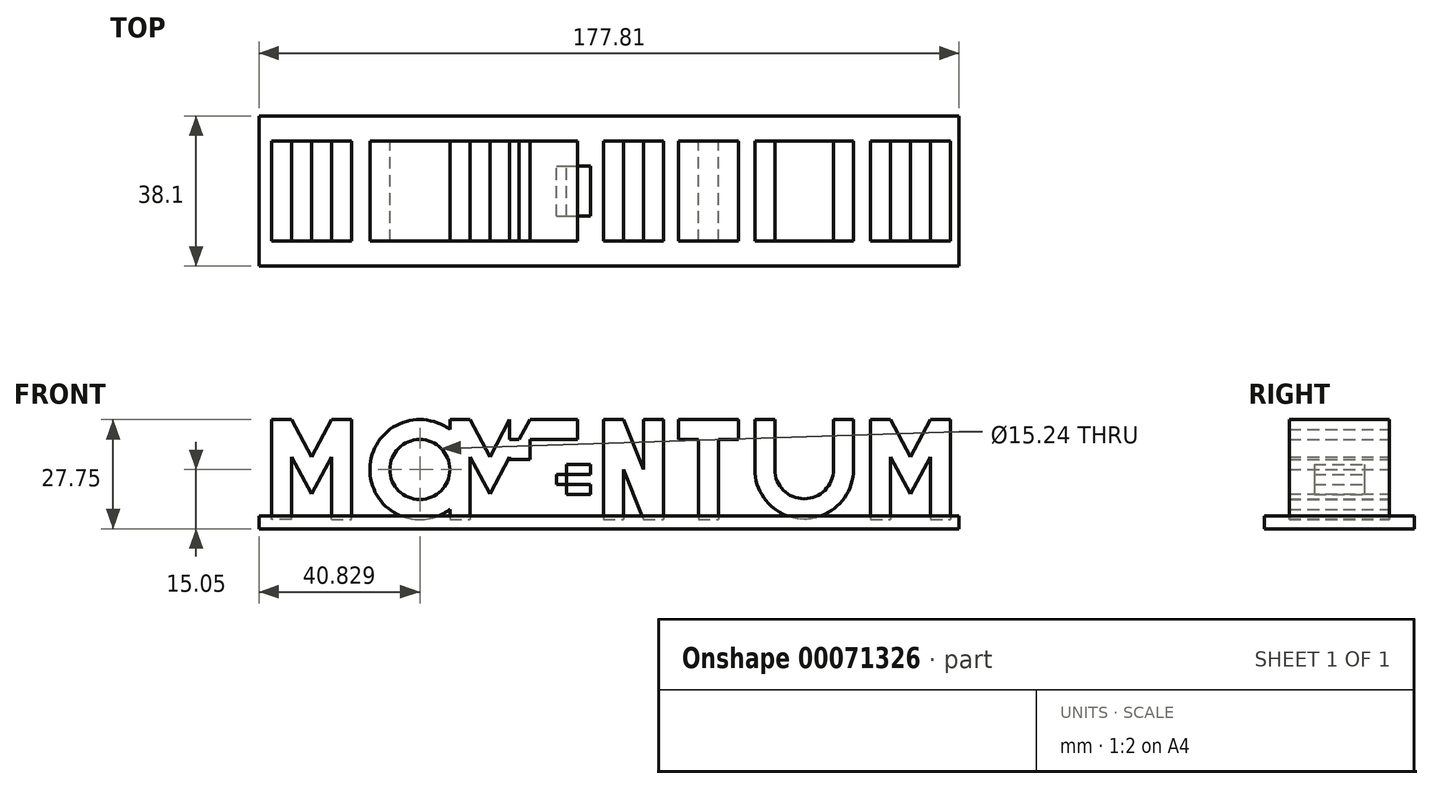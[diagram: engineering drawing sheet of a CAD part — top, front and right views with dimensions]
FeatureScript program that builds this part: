
annotation { "Feature Type Name" : "Feature", "Feature Type Description" : "" }
export const myFeature = defineFeature(function(context is Context, id is Id, definition is map)
    precondition{}
    {
        {
            var Q0;
            Q0=qCreatedBy(makeId("Front.planeOp"),FACE);
            var sketch = newSketch(context, id + "F0", { "sketchPlane" : qUnion([Q0])});
            skLineSegment(sketch, "E0.rect.bottom", {"start": v(-39.63, -6.35) * mm, "end": v(-42.17, -6.35) * mm});
            skLineSegment(sketch, "E0.rect.top", {"start": v(-39.63, 6.35) * mm, "end": v(-42.17, 6.35) * mm});
            skLineSegment(sketch, "E0.rect.left", {"start": v(-39.63, -6.35) * mm, "end": v(-39.63, 6.35) * mm});
            skLineSegment(sketch, "E0.rect.right", {"start": v(-42.17, -6.35) * mm, "end": v(-42.17, 6.35) * mm});
            skPoint(sketch, "E0.rect.middle", {"position": v(-40.9, 0) * mm});
            skLineSegment(sketch, "E1", {"start": v(-42.17, 6.35) * mm, "end": v(3.15, 6.35) * mm});
            skPoint(sketch, "E1.endSnap0", {"position": v(-40.9, 6.35) * mm});
            skLineSegment(sketch, "E2", {"start": v(-42.17, -6.35) * mm, "end": v(48.91, -6.35) * mm});
            skPoint(sketch, "E2.endSnap0", {"position": v(-40.9, -6.35) * mm});
            skLineSegment(sketch, "E3", {"start": v(-37.1, 6.35) * mm, "end": v(-37.1, -6.35) * mm});
            skLineSegment(sketch, "E4.MirrorCS", {"start": v(-34.55, -6.35) * mm, "end": v(-34.55, 6.35) * mm});
            skLineSegment(sketch, "E5.MirrorCS", {"start": v(-32.01, -6.35) * mm, "end": v(-32.01, 6.35) * mm});
            skLineSegment(sketch, "E6", {"start": v(-42.17, 6.35) * mm, "end": v(-37.1, -3.1) * mm});
            skLineSegment(sketch, "E7", {"start": v(-39.63, 6.35) * mm, "end": v(-37.1, 1.63) * mm});
            skLineSegment(sketch, "E8", {"start": v(-37.1, 1.63) * mm, "end": v(-34.55, 6.35) * mm});
            skLineSegment(sketch, "E9", {"start": v(-32.01, 6.35) * mm, "end": v(-37.1, -3.1) * mm});
            skCircle(sketch, "E10", {"center": v(-23.32, 0) * mm, "radius": 6.35 * mm});
            skCircle(sketch, "E11", {"center": v(-23.32, 0) * mm, "radius": 3.8 * mm});
            skLineSegment(sketch, "E12", {"start": v(-19.51, 0) * mm, "end": v(-16.97, 0) * mm});
            skLineSegment(sketch, "E13", {"start": v(-19.51, 6.35) * mm, "end": v(-19.51, -6.35) * mm});
            skLineSegment(sketch, "E14", {"start": v(-16.97, 6.35) * mm, "end": v(-16.97, -6.35) * mm});
            skLineSegment(sketch, "E15", {"start": v(-14.43, 6.35) * mm, "end": v(-14.43, -6.35) * mm});
            skLineSegment(sketch, "E16", {"start": v(-11.9, 6.35) * mm, "end": v(-11.9, -6.35) * mm});
            skLineSegment(sketch, "E17", {"start": v(-9.35, 6.35) * mm, "end": v(-9.35, -6.35) * mm});
            skLineSegment(sketch, "E18", {"start": v(-19.51, 6.35) * mm, "end": v(-14.43, -3.1) * mm});
            skLineSegment(sketch, "E19", {"start": v(-14.43, -3.1) * mm, "end": v(-9.35, 6.35) * mm});
            skLineSegment(sketch, "E20", {"start": v(-16.97, 6.35) * mm, "end": v(-14.43, 1.62) * mm});
            skLineSegment(sketch, "E21", {"start": v(-14.43, 1.62) * mm, "end": v(-11.9, 6.35) * mm});
            skLineSegment(sketch, "E22", {"start": v(3.15, 6.35) * mm, "end": v(48.32, 6.35) * mm});
            skLineSegment(sketch, "E23.bottom", {"start": v(-11.9, 6.35) * mm, "end": v(-3.3, 6.35) * mm});
            skLineSegment(sketch, "E23.top", {"start": v(-11.9, 3.81) * mm, "end": v(-3.3, 3.81) * mm});
            skLineSegment(sketch, "E23.left", {"start": v(-11.9, 6.35) * mm, "end": v(-11.9, 3.81) * mm});
            skLineSegment(sketch, "E23.right", {"start": v(-3.3, 6.35) * mm, "end": v(-3.3, 3.81) * mm});
            skLineSegment(sketch, "E24.bottom", {"start": v(-11.9, 1.27) * mm, "end": v(-3.3, 1.27) * mm});
            skLineSegment(sketch, "E24.top", {"start": v(-11.9, -1.27) * mm, "end": v(-3.3, -1.27) * mm});
            skLineSegment(sketch, "E24.left", {"start": v(-11.9, 1.27) * mm, "end": v(-11.9, -1.27) * mm});
            skLineSegment(sketch, "E24.right", {"start": v(-3.3, 1.27) * mm, "end": v(-3.3, -1.27) * mm});
            skLineSegment(sketch, "E25.bottom", {"start": v(-11.9, -6.35) * mm, "end": v(-3.3, -6.35) * mm});
            skLineSegment(sketch, "E25.top", {"start": v(-11.9, -3.8) * mm, "end": v(-3.3, -3.8) * mm});
            skLineSegment(sketch, "E25.left", {"start": v(-11.9, -6.35) * mm, "end": v(-11.9, -3.8) * mm});
            skLineSegment(sketch, "E25.right", {"start": v(-3.3, -6.35) * mm, "end": v(-3.3, -3.8) * mm});
            skLineSegment(sketch, "E26", {"start": v(0, 6.35) * mm, "end": v(0, -6.35) * mm});
            skLineSegment(sketch, "E27", {"start": v(2.54, 6.35) * mm, "end": v(2.54, -6.35) * mm});
            skLineSegment(sketch, "E28", {"start": v(5.08, 6.35) * mm, "end": v(5.08, -6.35) * mm});
            skLineSegment(sketch, "E29", {"start": v(7.62, 6.35) * mm, "end": v(7.62, -6.35) * mm});
            skLineSegment(sketch, "E30", {"start": v(0, 6.35) * mm, "end": v(5.08, -6.35) * mm});
            skLineSegment(sketch, "E31", {"start": v(2.54, 6.35) * mm, "end": v(7.62, -6.35) * mm});
            skLineSegment(sketch, "E32.bottom", {"start": v(12.07, 6.35) * mm, "end": v(14.6, 6.35) * mm});
            skLineSegment(sketch, "E32.top", {"start": v(12.07, -6.35) * mm, "end": v(14.6, -6.35) * mm});
            skLineSegment(sketch, "E32.left", {"start": v(12.07, 6.35) * mm, "end": v(12.07, -6.35) * mm});
            skLineSegment(sketch, "E32.right", {"start": v(14.6, 6.35) * mm, "end": v(14.6, -6.35) * mm});
            skLineSegment(sketch, "E33.bottom", {"start": v(9.53, 6.35) * mm, "end": v(17.15, 6.35) * mm});
            skLineSegment(sketch, "E33.top", {"start": v(9.53, 3.81) * mm, "end": v(17.15, 3.81) * mm});
            skLineSegment(sketch, "E33.left", {"start": v(9.53, 6.35) * mm, "end": v(9.53, 3.81) * mm});
            skLineSegment(sketch, "E33.right", {"start": v(17.15, 6.35) * mm, "end": v(17.15, 3.81) * mm});
            skArc(sketch, "E34", {"start": v(19.25, 0) * mm, "mid": v(25.5, -6.25) * mm, "end": v(31.76, 0) * mm});
            skArc(sketch, "E35", {"start": v(21.79, 0) * mm, "mid": v(25.5, -3.71) * mm, "end": v(29.22, 0) * mm});
            skLineSegment(sketch, "E36", {"start": v(19.25, 0) * mm, "end": v(19.25, 6.35) * mm});
            skLineSegment(sketch, "E37", {"start": v(21.79, 0) * mm, "end": v(21.79, 6.35) * mm});
            skLineSegment(sketch, "E38", {"start": v(29.22, 0) * mm, "end": v(29.22, 6.35) * mm});
            skLineSegment(sketch, "E39", {"start": v(31.76, 0) * mm, "end": v(31.76, 6.35) * mm});
            skLineSegment(sketch, "E40", {"start": v(33.92, 6.35) * mm, "end": v(33.92, -6.35) * mm});
            skLineSegment(sketch, "E41", {"start": v(36.46, 6.35) * mm, "end": v(36.46, -6.35) * mm});
            skLineSegment(sketch, "E42", {"start": v(39, 6.35) * mm, "end": v(39, -6.35) * mm});
            skLineSegment(sketch, "E43", {"start": v(41.54, 6.35) * mm, "end": v(41.54, -6.35) * mm});
            skLineSegment(sketch, "E44", {"start": v(44.08, 6.35) * mm, "end": v(44.08, -6.35) * mm});
            skLineSegment(sketch, "E45", {"start": v(33.92, 6.35) * mm, "end": v(39, -3.1) * mm});
            skLineSegment(sketch, "E46", {"start": v(39, -3.1) * mm, "end": v(44.08, 6.35) * mm});
            skLineSegment(sketch, "E47", {"start": v(36.46, 6.35) * mm, "end": v(39, 1.63) * mm});
            skLineSegment(sketch, "E48", {"start": v(39, 1.63) * mm, "end": v(41.54, 6.35) * mm});
            skSolve(sketch);
        }
        {
            var Q0;
            {var subQ5=sQuery(id+"F0.wireOp",EDGE,"E0.rect.right");Q0=makeQuery(id+"F0.imprint","IMPRINT",FACE,{"disambiguationData":[TD([[makeQuery(id+"F0.imprint","IMPRINT",EDGE,{"derivedFrom":subQ5}),-1.0]])]});}
            var Q1;
            {var subQ1=sQuery(id+"F0.wireOp",EDGE,"E0.rect.left");var subQ3=sQuery(id+"F0.wireOp",EDGE,"E6");var subQ4=makeQuery(id+"F0.imprint","INTERSECT",VERTEX,{"derivedFrom":[subQ1,subQ3]});Q1=makeQuery(id+"F0.imprint","IMPRINT",FACE,{"disambiguationData":[TD([[makeQuery(id+"F0.imprint","IMPRINT",EDGE,{"disambiguationData":[TD([[subQ4,-1.0]])],"derivedFrom":subQ1}),1.0]])]});}
            var Q2;
            {var subQ0=sQuery(id+"F0.wireOp",EDGE,"E7");Q2=makeQuery(id+"F0.imprint","IMPRINT",FACE,{"disambiguationData":[TD([[makeQuery(id+"F0.imprint","IMPRINT",EDGE,{"derivedFrom":subQ0}),-1.0]])]});}
            var Q3;
            {var subQ3=sQuery(id+"F0.wireOp",EDGE,"E8");Q3=makeQuery(id+"F0.imprint","IMPRINT",FACE,{"disambiguationData":[TD([[makeQuery(id+"F0.imprint","IMPRINT",EDGE,{"derivedFrom":subQ3}),-1.0]])]});}
            var Q4;
            {var subQ0=sQuery(id+"F0.wireOp",EDGE,"E4.MirrorCS");var subQ3=sQuery(id+"F0.wireOp",EDGE,"E9");var subQ5=makeQuery(id+"F0.imprint","INTERSECT",VERTEX,{"derivedFrom":[subQ0,subQ3]});Q4=makeQuery(id+"F0.imprint","IMPRINT",FACE,{"disambiguationData":[TD([[makeQuery(id+"F0.imprint","IMPRINT",EDGE,{"disambiguationData":[TD([[subQ5,-1.0]])],"derivedFrom":subQ0}),-1.0]])]});}
            var Q5;
            {var subQ3=sQuery(id+"F0.wireOp",EDGE,"E5.MirrorCS");Q5=makeQuery(id+"F0.imprint","IMPRINT",FACE,{"disambiguationData":[TD([[makeQuery(id+"F0.imprint","IMPRINT",EDGE,{"derivedFrom":subQ3}),1.0]])]});}
            var Q6;
            {var subQ0=sQuery(id+"F0.wireOp",EDGE,"E11");Q6=makeQuery(id+"F0.imprint","IMPRINT",FACE,{"disambiguationData":[TD([[makeQuery(id+"F0.imprint","IMPRINT",EDGE,{"derivedFrom":subQ0}),-1.0]])]});}
            var Q7;
            {var subQ0=sQuery(id+"F0.wireOp",EDGE,"E12");Q7=makeQuery(id+"F0.imprint","IMPRINT",FACE,{"disambiguationData":[TD([[makeQuery(id+"F0.imprint","IMPRINT",EDGE,{"derivedFrom":subQ0}),1.0]])]});}
            var Q8;
            {var subQ0=sQuery(id+"F0.wireOp",EDGE,"E12");Q8=makeQuery(id+"F0.imprint","IMPRINT",FACE,{"disambiguationData":[TD([[makeQuery(id+"F0.imprint","IMPRINT",EDGE,{"derivedFrom":subQ0}),-1.0]])]});}
            var Q9;
            {var subQ0=sQuery(id+"F0.wireOp",EDGE,"E13");var subQ1=sQuery(id+"F0.wireOp",EDGE,"E2");var subQ2=makeQuery(id+"F0.imprint","INTERSECT",VERTEX,{"derivedFrom":[subQ1,subQ0]});Q9=makeQuery(id+"F0.imprint","IMPRINT",FACE,{"disambiguationData":[TD([[makeQuery(id+"F0.imprint","IMPRINT",EDGE,{"disambiguationData":[TD([[subQ2,-1.0]])],"derivedFrom":subQ1}),1.0]])]});}
            var Q10;
            {var subQ0=sQuery(id+"F0.wireOp",EDGE,"E18");var subQ3=sQuery(id+"F0.wireOp",EDGE,"E14");var subQ5=makeQuery(id+"F0.imprint","INTERSECT",VERTEX,{"derivedFrom":[subQ3,subQ0]});Q10=makeQuery(id+"F0.imprint","IMPRINT",FACE,{"disambiguationData":[TD([[makeQuery(id+"F0.imprint","IMPRINT",EDGE,{"disambiguationData":[TD([[subQ5,1.0]])],"derivedFrom":subQ3}),-1.0]])]});}
            var Q11;
            {var subQ1=sQuery(id+"F0.wireOp",EDGE,"E10");var subQ3=sQuery(id+"F0.wireOp",EDGE,"E13");var subQ4=makeQuery(id+"F0.imprint","INTERSECT",VERTEX,{"disambiguationData":[OD(0.0)],"derivedFrom":[subQ1,subQ3]});Q11=makeQuery(id+"F0.imprint","IMPRINT",FACE,{"disambiguationData":[TD([[makeQuery(id+"F0.imprint","IMPRINT",EDGE,{"disambiguationData":[TD([[subQ4,1.0]])],"derivedFrom":subQ1}),-1.0]])]});}
            var Q12;
            {var subQ0=sQuery(id+"F0.wireOp",EDGE,"E20");Q12=makeQuery(id+"F0.imprint","IMPRINT",FACE,{"disambiguationData":[TD([[makeQuery(id+"F0.imprint","IMPRINT",EDGE,{"derivedFrom":subQ0}),-1.0]])]});}
            var Q13;
            {var subQ5=sQuery(id+"F0.wireOp",EDGE,"E21");Q13=makeQuery(id+"F0.imprint","IMPRINT",FACE,{"disambiguationData":[TD([[makeQuery(id+"F0.imprint","IMPRINT",EDGE,{"derivedFrom":subQ5}),-1.0]])]});}
            var Q14;
            {var subQ5=sQuery(id+"F0.wireOp",EDGE,"E23.left");Q14=makeQuery(id+"F0.imprint","IMPRINT",FACE,{"disambiguationData":[TD([[makeQuery(id+"F0.imprint","IMPRINT",EDGE,{"derivedFrom":subQ5}),1.0]])]});}
            var Q15;
            {var subQ1=sQuery(id+"F0.wireOp",EDGE,"E16");var subQ3=sQuery(id+"F0.wireOp",EDGE,"E19");var subQ4=makeQuery(id+"F0.imprint","INTERSECT",VERTEX,{"derivedFrom":[subQ1,subQ3]});Q15=makeQuery(id+"F0.imprint","IMPRINT",FACE,{"disambiguationData":[TD([[makeQuery(id+"F0.imprint","IMPRINT",EDGE,{"disambiguationData":[TD([[subQ4,-1.0]])],"derivedFrom":subQ3}),1.0]])]});}
            var Q16;
            {var subQ5=sQuery(id+"F0.wireOp",EDGE,"E23.right");Q16=makeQuery(id+"F0.imprint","IMPRINT",FACE,{"disambiguationData":[TD([[makeQuery(id+"F0.imprint","IMPRINT",EDGE,{"derivedFrom":subQ5}),-1.0]])]});}
            var Q17;
            {var subQ0=sQuery(id+"F0.wireOp",EDGE,"E23.top");var subQ1=sQuery(id+"F0.wireOp",EDGE,"E17");var subQ2=makeQuery(id+"F0.imprint","INTERSECT",VERTEX,{"derivedFrom":[subQ1,subQ0]});Q17=makeQuery(id+"F0.imprint","IMPRINT",FACE,{"disambiguationData":[TD([[makeQuery(id+"F0.imprint","IMPRINT",EDGE,{"disambiguationData":[TD([[subQ2,-1.0]])],"derivedFrom":subQ1}),-1.0]])]});}
            var Q18;
            {var subQ1=sQuery(id+"F0.wireOp",EDGE,"E17");var subQ3=sQuery(id+"F0.wireOp",EDGE,"E23.top");var subQ4=makeQuery(id+"F0.imprint","INTERSECT",VERTEX,{"derivedFrom":[subQ1,subQ3]});Q18=makeQuery(id+"F0.imprint","IMPRINT",FACE,{"disambiguationData":[TD([[makeQuery(id+"F0.imprint","IMPRINT",EDGE,{"disambiguationData":[TD([[subQ4,1.0]])],"derivedFrom":subQ3}),1.0]])]});}
            var Q19;
            {var subQ5=sQuery(id+"F0.wireOp",EDGE,"E24.left");Q19=makeQuery(id+"F0.imprint","IMPRINT",FACE,{"disambiguationData":[TD([[makeQuery(id+"F0.imprint","IMPRINT",EDGE,{"derivedFrom":subQ5}),1.0]])]});}
            var Q20;
            {var subQ5=sQuery(id+"F0.wireOp",EDGE,"E24.right");Q20=makeQuery(id+"F0.imprint","IMPRINT",FACE,{"disambiguationData":[TD([[makeQuery(id+"F0.imprint","IMPRINT",EDGE,{"derivedFrom":subQ5}),-1.0]])]});}
            var Q21;
            {var subQ3=sQuery(id+"F0.wireOp",EDGE,"E24.top");var subQ5=sQuery(id+"F0.wireOp",EDGE,"E17");var subQ6=makeQuery(id+"F0.imprint","INTERSECT",VERTEX,{"derivedFrom":[subQ5,subQ3]});Q21=makeQuery(id+"F0.imprint","IMPRINT",FACE,{"disambiguationData":[TD([[makeQuery(id+"F0.imprint","IMPRINT",EDGE,{"disambiguationData":[TD([[subQ6,-1.0]])],"derivedFrom":subQ5}),-1.0]])]});}
            var Q22;
            {var subQ5=sQuery(id+"F0.wireOp",EDGE,"E25.left");Q22=makeQuery(id+"F0.imprint","IMPRINT",FACE,{"disambiguationData":[TD([[makeQuery(id+"F0.imprint","IMPRINT",EDGE,{"derivedFrom":subQ5}),-1.0]])]});}
            var Q23;
            {var subQ5=sQuery(id+"F0.wireOp",EDGE,"E25.right");Q23=makeQuery(id+"F0.imprint","IMPRINT",FACE,{"disambiguationData":[TD([[makeQuery(id+"F0.imprint","IMPRINT",EDGE,{"derivedFrom":subQ5}),1.0]])]});}
            var Q24;
            {var subQ0=sQuery(id+"F0.wireOp",EDGE,"E26");Q24=makeQuery(id+"F0.imprint","IMPRINT",FACE,{"disambiguationData":[TD([[makeQuery(id+"F0.imprint","IMPRINT",EDGE,{"derivedFrom":subQ0}),1.0]])]});}
            var Q25;
            {var subQ0=sQuery(id+"F0.wireOp",EDGE,"E30");var subQ3=sQuery(id+"F0.wireOp",EDGE,"E27");var subQ5=makeQuery(id+"F0.imprint","INTERSECT",VERTEX,{"derivedFrom":[subQ3,subQ0]});Q25=makeQuery(id+"F0.imprint","IMPRINT",FACE,{"disambiguationData":[TD([[makeQuery(id+"F0.imprint","IMPRINT",EDGE,{"disambiguationData":[TD([[subQ5,1.0]])],"derivedFrom":subQ3}),-1.0]])]});}
            var Q26;
            {var subQ1=sQuery(id+"F0.wireOp",EDGE,"E27");var subQ3=sQuery(id+"F0.wireOp",EDGE,"E30");var subQ4=makeQuery(id+"F0.imprint","INTERSECT",VERTEX,{"derivedFrom":[subQ1,subQ3]});Q26=makeQuery(id+"F0.imprint","IMPRINT",FACE,{"disambiguationData":[TD([[makeQuery(id+"F0.imprint","IMPRINT",EDGE,{"disambiguationData":[TD([[subQ4,1.0]])],"derivedFrom":subQ1}),1.0]])]});}
            var Q27;
            {var subQ0=sQuery(id+"F0.wireOp",EDGE,"E28");var subQ3=sQuery(id+"F0.wireOp",EDGE,"E31");var subQ5=makeQuery(id+"F0.imprint","INTERSECT",VERTEX,{"derivedFrom":[subQ0,subQ3]});Q27=makeQuery(id+"F0.imprint","IMPRINT",FACE,{"disambiguationData":[TD([[makeQuery(id+"F0.imprint","IMPRINT",EDGE,{"disambiguationData":[TD([[subQ5,-1.0]])],"derivedFrom":subQ0}),1.0]])]});}
            var Q28;
            {var subQ3=sQuery(id+"F0.wireOp",EDGE,"E29");Q28=makeQuery(id+"F0.imprint","IMPRINT",FACE,{"disambiguationData":[TD([[makeQuery(id+"F0.imprint","IMPRINT",EDGE,{"derivedFrom":subQ3}),-1.0]])]});}
            var Q29;
            {var subQ0=sQuery(id+"F0.wireOp",EDGE,"E32.top");Q29=makeQuery(id+"F0.imprint","IMPRINT",FACE,{"disambiguationData":[TD([[makeQuery(id+"F0.imprint","IMPRINT",EDGE,{"derivedFrom":subQ0}),1.0]])]});}
            var Q30;
            {var subQ5=sQuery(id+"F0.wireOp",EDGE,"E33.right");Q30=makeQuery(id+"F0.imprint","IMPRINT",FACE,{"disambiguationData":[TD([[makeQuery(id+"F0.imprint","IMPRINT",EDGE,{"derivedFrom":subQ5}),-1.0]])]});}
            var Q31;
            {var subQ0=sQuery(id+"F0.wireOp",EDGE,"E33.bottom");var subQ1=sQuery(id+"F0.wireOp",EDGE,"E32.left");var subQ2=makeQuery(id+"F0.imprint","INTERSECT",VERTEX,{"derivedFrom":[subQ1,subQ0]});Q31=makeQuery(id+"F0.imprint","IMPRINT",FACE,{"disambiguationData":[TD([[makeQuery(id+"F0.imprint","IMPRINT",EDGE,{"disambiguationData":[TD([[subQ2,-1.0]])],"derivedFrom":subQ1}),1.0]])]});}
            var Q32;
            {var subQ5=sQuery(id+"F0.wireOp",EDGE,"E33.left");Q32=makeQuery(id+"F0.imprint","IMPRINT",FACE,{"disambiguationData":[TD([[makeQuery(id+"F0.imprint","IMPRINT",EDGE,{"derivedFrom":subQ5}),1.0]])]});}
            var Q33;
            Q33=makeQuery(id+"F0.imprint","IMPRINT",FACE,{"disambiguationData":[TD([[makeQuery(id+"F0.imprint","IMPRINT",EDGE,{"derivedFrom":sQuery(id+"F0.wireOp",EDGE,"E34")}),1.0]])]});
            var Q34;
            {var subQ0=sQuery(id+"F0.wireOp",EDGE,"E40");Q34=makeQuery(id+"F0.imprint","IMPRINT",FACE,{"disambiguationData":[TD([[makeQuery(id+"F0.imprint","IMPRINT",EDGE,{"derivedFrom":subQ0}),1.0]])]});}
            var Q35;
            {var subQ0=sQuery(id+"F0.wireOp",EDGE,"E45");var subQ3=sQuery(id+"F0.wireOp",EDGE,"E41");var subQ5=makeQuery(id+"F0.imprint","INTERSECT",VERTEX,{"derivedFrom":[subQ3,subQ0]});Q35=makeQuery(id+"F0.imprint","IMPRINT",FACE,{"disambiguationData":[TD([[makeQuery(id+"F0.imprint","IMPRINT",EDGE,{"disambiguationData":[TD([[subQ5,1.0]])],"derivedFrom":subQ3}),-1.0]])]});}
            var Q36;
            {var subQ0=sQuery(id+"F0.wireOp",EDGE,"E47");Q36=makeQuery(id+"F0.imprint","IMPRINT",FACE,{"disambiguationData":[TD([[makeQuery(id+"F0.imprint","IMPRINT",EDGE,{"derivedFrom":subQ0}),-1.0]])]});}
            var Q37;
            {var subQ3=sQuery(id+"F0.wireOp",EDGE,"E48");Q37=makeQuery(id+"F0.imprint","IMPRINT",FACE,{"disambiguationData":[TD([[makeQuery(id+"F0.imprint","IMPRINT",EDGE,{"derivedFrom":subQ3}),-1.0]])]});}
            var Q38;
            {var subQ0=sQuery(id+"F0.wireOp",EDGE,"E43");var subQ3=sQuery(id+"F0.wireOp",EDGE,"E46");var subQ5=makeQuery(id+"F0.imprint","INTERSECT",VERTEX,{"derivedFrom":[subQ0,subQ3]});Q38=makeQuery(id+"F0.imprint","IMPRINT",FACE,{"disambiguationData":[TD([[makeQuery(id+"F0.imprint","IMPRINT",EDGE,{"disambiguationData":[TD([[subQ5,1.0]])],"derivedFrom":subQ0}),1.0]])]});}
            var Q39;
            {var subQ3=sQuery(id+"F0.wireOp",EDGE,"E44");Q39=makeQuery(id+"F0.imprint","IMPRINT",FACE,{"disambiguationData":[TD([[makeQuery(id+"F0.imprint","IMPRINT",EDGE,{"derivedFrom":subQ3}),-1.0]])]});}
            extrude(context, id + "F1", {"entities" : qUnion([Q0, Q1, Q2, Q3, Q4, Q5, Q6, Q7, Q8, Q9, Q10, Q11, Q12, Q13, Q14, Q15, Q16, Q17, Q18, Q19, Q20, Q21, Q22, Q23, Q24, Q25, Q26, Q27, Q28, Q29, Q30, Q31, Q32, Q33, Q34, Q35, Q36, Q37, Q38, Q39]), "endBound" : BoundingType.SYMMETRIC, "depth" : 12.7 * mm});
        }
        {
            var Q0;
            Q0=qCreatedBy(makeId("Front.planeOp"),FACE);
            var sketch = newSketch(context, id + "F2", { "sketchPlane" : qUnion([Q0])});
            skLineSegment(sketch, "E49.bottom", {"start": v(-43.73, -5.87) * mm, "end": v(45.17, -5.87) * mm});
            skLineSegment(sketch, "E49.top", {"start": v(-43.73, -7.53) * mm, "end": v(45.17, -7.53) * mm});
            skLineSegment(sketch, "E49.left", {"start": v(-43.73, -5.87) * mm, "end": v(-43.73, -7.53) * mm});
            skLineSegment(sketch, "E49.right", {"start": v(45.17, -5.87) * mm, "end": v(45.17, -7.53) * mm});
            skSolve(sketch);
        }
        {
            var Q0;
            Q0=makeQuery(id+"F2.imprint","IMPRINT",FACE,{"disambiguationData":[TD([[makeQuery(id+"F2.imprint","IMPRINT",EDGE,{"derivedFrom":sQuery(id+"F2.wireOp",EDGE,"E49.bottom")}),-1.0]])]});
            extrude(context, id + "F3", {"entities" : qUnion([Q0]), "endBound" : BoundingType.SYMMETRIC, "depth" : 19.05 * mm});
        }
        {
            var Q0;
            Q0=makeQuery(id+"F1.opExtrude","SWEPT_BODY",BODY,{"disambiguationData":[OSD([sQuery(id+"F0.wireOp",EDGE,"E32.top"),sQuery(id+"F0.wireOp",EDGE,"E32.left"),sQuery(id+"F0.wireOp",EDGE,"E32.right"),sQuery(id+"F0.wireOp",EDGE,"E33.bottom"),sQuery(id+"F0.wireOp",EDGE,"E33.top"),sQuery(id+"F0.wireOp",EDGE,"E33.left"),sQuery(id+"F0.wireOp",EDGE,"E33.right")])]});
            var Q1;
            Q1=makeQuery(id+"F1.opExtrude","SWEPT_BODY",BODY,{"disambiguationData":[OSD([sQuery(id+"F0.wireOp",EDGE,"E0.rect.left"),sQuery(id+"F0.wireOp",EDGE,"E0.rect.right"),sQuery(id+"F0.wireOp",EDGE,"E1"),sQuery(id+"F0.wireOp",EDGE,"E2"),sQuery(id+"F0.wireOp",EDGE,"E4.MirrorCS"),sQuery(id+"F0.wireOp",EDGE,"E5.MirrorCS"),sQuery(id+"F0.wireOp",EDGE,"E6"),sQuery(id+"F0.wireOp",EDGE,"E7"),sQuery(id+"F0.wireOp",EDGE,"E8"),sQuery(id+"F0.wireOp",EDGE,"E9")])]});
            var Q2;
            Q2=makeQuery(id+"F1.opExtrude","SWEPT_BODY",BODY,{"disambiguationData":[OSD([sQuery(id+"F0.wireOp",EDGE,"E1"),sQuery(id+"F0.wireOp",EDGE,"E2"),sQuery(id+"F0.wireOp",EDGE,"E10"),sQuery(id+"F0.wireOp",EDGE,"E11"),sQuery(id+"F0.wireOp",EDGE,"E13"),sQuery(id+"F0.wireOp",EDGE,"E14"),sQuery(id+"F0.wireOp",EDGE,"E16"),sQuery(id+"F0.wireOp",EDGE,"E17"),sQuery(id+"F0.wireOp",EDGE,"E18"),sQuery(id+"F0.wireOp",EDGE,"E19"),sQuery(id+"F0.wireOp",EDGE,"E20"),sQuery(id+"F0.wireOp",EDGE,"E21"),sQuery(id+"F0.wireOp",EDGE,"E23.bottom"),sQuery(id+"F0.wireOp",EDGE,"E23.top"),sQuery(id+"F0.wireOp",EDGE,"E23.right"),sQuery(id+"F0.wireOp",EDGE,"E24.bottom"),sQuery(id+"F0.wireOp",EDGE,"E24.top"),sQuery(id+"F0.wireOp",EDGE,"E24.left"),sQuery(id+"F0.wireOp",EDGE,"E24.right"),sQuery(id+"F0.wireOp",EDGE,"E25.bottom"),sQuery(id+"F0.wireOp",EDGE,"E25.top"),sQuery(id+"F0.wireOp",EDGE,"E25.left"),sQuery(id+"F0.wireOp",EDGE,"E25.right")])]});
            var Q3;
            Q3=makeQuery(id+"F1.opExtrude","SWEPT_BODY",BODY,{"disambiguationData":[OSD([sQuery(id+"F0.wireOp",EDGE,"E1"),sQuery(id+"F0.wireOp",EDGE,"E2"),sQuery(id+"F0.wireOp",EDGE,"E22"),sQuery(id+"F0.wireOp",EDGE,"E26"),sQuery(id+"F0.wireOp",EDGE,"E27"),sQuery(id+"F0.wireOp",EDGE,"E28"),sQuery(id+"F0.wireOp",EDGE,"E29"),sQuery(id+"F0.wireOp",EDGE,"E30"),sQuery(id+"F0.wireOp",EDGE,"E31")])]});
            var Q4;
            Q4=makeQuery(id+"F1.opExtrude","SWEPT_BODY",BODY,{"disambiguationData":[OSD([sQuery(id+"F0.wireOp",EDGE,"E22"),sQuery(id+"F0.wireOp",EDGE,"E34"),sQuery(id+"F0.wireOp",EDGE,"E35"),sQuery(id+"F0.wireOp",EDGE,"E36"),sQuery(id+"F0.wireOp",EDGE,"E37"),sQuery(id+"F0.wireOp",EDGE,"E38"),sQuery(id+"F0.wireOp",EDGE,"E39")])]});
            var Q5;
            Q5=makeQuery(id+"F1.opExtrude","SWEPT_BODY",BODY,{"disambiguationData":[OSD([sQuery(id+"F0.wireOp",EDGE,"E2"),sQuery(id+"F0.wireOp",EDGE,"E22"),sQuery(id+"F0.wireOp",EDGE,"E40"),sQuery(id+"F0.wireOp",EDGE,"E41"),sQuery(id+"F0.wireOp",EDGE,"E43"),sQuery(id+"F0.wireOp",EDGE,"E44"),sQuery(id+"F0.wireOp",EDGE,"E45"),sQuery(id+"F0.wireOp",EDGE,"E46"),sQuery(id+"F0.wireOp",EDGE,"E47"),sQuery(id+"F0.wireOp",EDGE,"E48")])]});
            var Q6;
            Q6=makeQuery(id+"F3.opExtrude","SWEPT_BODY",BODY,{"disambiguationData":[OSD([sQuery(id+"F2.wireOp",EDGE,"E49.bottom"),sQuery(id+"F2.wireOp",EDGE,"E49.top"),sQuery(id+"F2.wireOp",EDGE,"E49.left"),sQuery(id+"F2.wireOp",EDGE,"E49.right")])]});
            var Q7;
            Q7=qCreatedBy(makeId("Origin.pointOp"),VERTEX);
            transform(context, id + "F4", {"entities" : qUnion([Q0, Q1, Q2, Q3, Q4, Q5, Q6]), "transformType" : TransformType.SCALE_UNIFORMLY, "scale" : 2, "scalePoint" : qUnion([Q7]), "makeCopy" : false});
        }
    });
